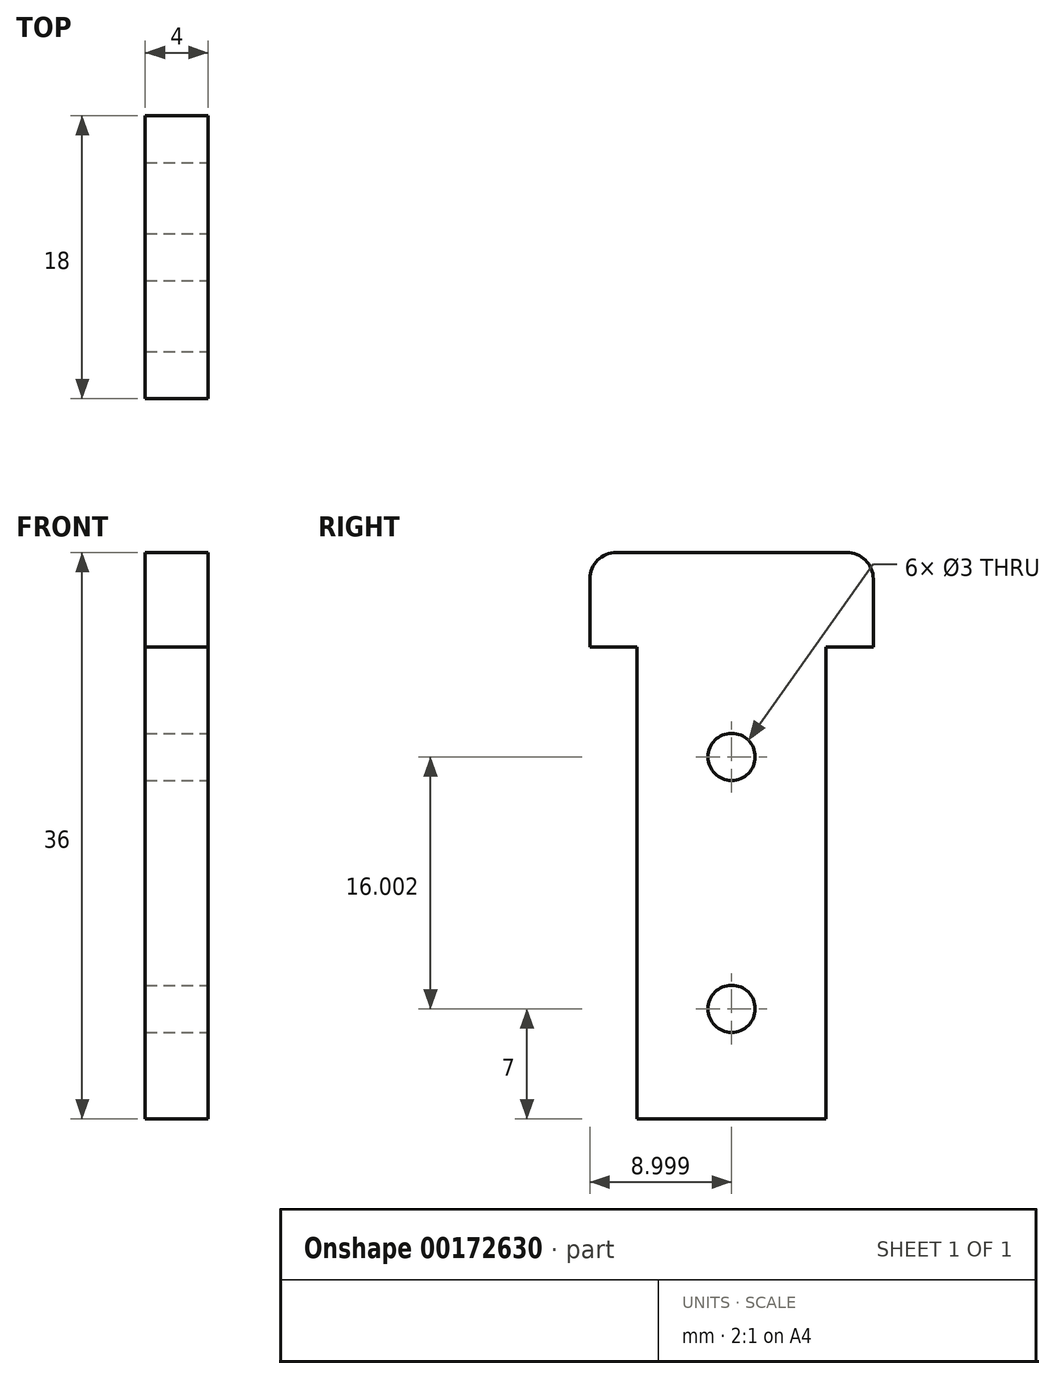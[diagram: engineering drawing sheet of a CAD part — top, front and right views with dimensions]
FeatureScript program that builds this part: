
annotation { "Feature Type Name" : "Feature", "Feature Type Description" : "" }
export const myFeature = defineFeature(function(context is Context, id is Id, definition is map)
    precondition{}
    {
        {
            var Q0;
            Q0=qCreatedBy(makeId("Top.planeOp"),FACE);
            var sketch = newSketch(context, id + "F0", { "sketchPlane" : qUnion([Q0])});
            skLineSegment(sketch, "E0.top", {"start": v(-6, -16.07) * mm, "end": v(6, -16.07) * mm});
            skLineSegment(sketch, "E0.left", {"start": v(-6, 13.93) * mm, "end": v(-6, -16.07) * mm});
            skLineSegment(sketch, "E0.right", {"start": v(6, 13.93) * mm, "end": v(6, -16.07) * mm});
            skLineSegment(sketch, "E1", {"start": v(-6, 13.93) * mm, "end": v(-9, 13.93) * mm});
            skLineSegment(sketch, "E2", {"start": v(-9, 13.93) * mm, "end": v(-9, 18.23) * mm});
            skLineSegment(sketch, "E3", {"start": v(-7.3, 19.93) * mm, "end": v(7.3, 19.93) * mm});
            skLineSegment(sketch, "E4", {"start": v(9, 18.23) * mm, "end": v(9, 13.93) * mm});
            skLineSegment(sketch, "E5", {"start": v(9, 13.93) * mm, "end": v(6, 13.93) * mm});
            skArc(sketch, "E6.filletArc", {"start": v(-7.3, 19.93) * mm, "mid": v(-8.5, 19.43) * mm, "end": v(-9, 18.23) * mm});
            skArc(sketch, "E7.filletArc", {"start": v(9, 18.23) * mm, "mid": v(8.5, 19.43) * mm, "end": v(7.3, 19.93) * mm});
            skPoint(sketch, "E8", {"position": v(0, -9.07) * mm});
            skPoint(sketch, "E9", {"position": v(0, 6.93) * mm});
            skCircle(sketch, "E10", {"center": v(0, 6.93) * mm, "radius": 1.5 * mm});
            skCircle(sketch, "E11", {"center": v(0, -9.07) * mm, "radius": 1.5 * mm});
            skSolve(sketch);
        }
        {
            var Q0;
            Q0 = qSketchRegion(id + "F0", true);
            extrude(context, id + "F1", {"entities" : qUnion([Q0]), "depth" : 4 * mm});
        }
        {
            var Q0;
            Q0=makeQuery(id+"F1.opExtrude","SWEPT_BODY",BODY,{"disambiguationData":[OSD([sQuery(id+"F0.wireOp",EDGE,"E0.top"),sQuery(id+"F0.wireOp",EDGE,"E0.left"),sQuery(id+"F0.wireOp",EDGE,"E0.right"),sQuery(id+"F0.wireOp",EDGE,"E1"),sQuery(id+"F0.wireOp",EDGE,"E2"),sQuery(id+"F0.wireOp",EDGE,"E3"),sQuery(id+"F0.wireOp",EDGE,"E4"),sQuery(id+"F0.wireOp",EDGE,"E5"),sQuery(id+"F0.wireOp",EDGE,"E6.filletArc"),sQuery(id+"F0.wireOp",EDGE,"E7.filletArc"),sQuery(id+"F0.wireOp",EDGE,"E10"),sQuery(id+"F0.wireOp",EDGE,"E11")])]});
            var Q1;
            Q1=makeQuery(id+"F1.opExtrude","CAP_EDGE",EDGE,{"disambiguationData":[OSD([sQuery(id+"F0.wireOp",EDGE,"E0.top")])],"isStart":true});
            transform(context, id + "F2", {"entities" : qUnion([Q0]), "transformType" : TransformType.ROTATION, "transformAxis" : qUnion([Q1]), "angle" : 90 * degree, "makeCopy" : false});
        }
        {
            var Q0;
            Q0=makeQuery(id+"F1.opExtrude","SWEPT_FACE",FACE,{"disambiguationData":[OSD([sQuery(id+"F0.wireOp",EDGE,"E0.right")])]});
            var sketch = newSketch(context, id + "F3", { "sketchPlane" : qUnion([Q0])});
            skLineSegment(sketch, "E12", {"start": v(-16.07, 27.68) * mm, "end": v(-16.07, -25.06) * mm, "construction": true});
            skSolve(sketch);
        }
        {
            var Q0;
            Q0=makeQuery(id+"F1.opExtrude","SWEPT_BODY",BODY,{"disambiguationData":[OSD([sQuery(id+"F0.wireOp",EDGE,"E0.top"),sQuery(id+"F0.wireOp",EDGE,"E0.left"),sQuery(id+"F0.wireOp",EDGE,"E0.right"),sQuery(id+"F0.wireOp",EDGE,"E1"),sQuery(id+"F0.wireOp",EDGE,"E2"),sQuery(id+"F0.wireOp",EDGE,"E3"),sQuery(id+"F0.wireOp",EDGE,"E4"),sQuery(id+"F0.wireOp",EDGE,"E5"),sQuery(id+"F0.wireOp",EDGE,"E6.filletArc"),sQuery(id+"F0.wireOp",EDGE,"E7.filletArc"),sQuery(id+"F0.wireOp",EDGE,"E10"),sQuery(id+"F0.wireOp",EDGE,"E11")])]});
            var Q1;
            Q1=sQuery(id+"F3.wireOp",EDGE,"E12");
            transform(context, id + "F4", {"entities" : qUnion([Q0]), "transformType" : TransformType.ROTATION, "transformAxis" : qUnion([Q1]), "angle" : 90 * degree, "makeCopy" : false});
        }
    });
